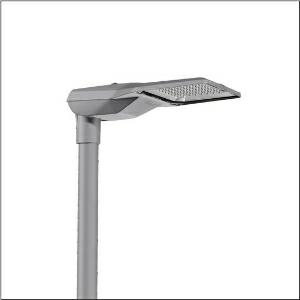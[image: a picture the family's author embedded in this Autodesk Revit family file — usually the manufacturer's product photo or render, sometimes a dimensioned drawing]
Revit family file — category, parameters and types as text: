
# Revit family: streetlight_sl_21_iq_midi___st1_0ab_5xe3m31v08nb_f534
name_source: partatom
category: Lighting Fixtures
units: mm (PartAtom-declared; Revit-internal decimal feet)

## family parameters
Cut with Voids When Loaded = No
Host = Face
Light Source = No
Part Type = Normal
Room Calculation Point = No
Round Connector Dimension = Use Diameter
Shared = No

## types (1)
- --- (1 x LED, 18970 lm, 136.6 W, 3000K)
    Apparent Load = 137 VA
    CIE Flux Codes = 40 74 97 100 100
    Color Rendering = 70
    Color Temperature = 3000K
    Default Elevation = 1800 mm
    Description = Streetlight SL 21 iQ midi, mast luminaire, primary light control with lens, of PMMA, primary optical cover: cover, of toughened safety glass, transparent, light distribution: ST1.0aB, light emission: direct distribution, primary light characteristic: asymmetric, installation type: post-top, side-entry, LED, High Power LED, rated luminous flux: 18.970lm, luminous efficacy: 139lm/W, light colour: 730, colour temperature: 3000K, control gear: iQ-Street Remote, D4i with power reduction, control: pre-setting: logarithmic dimming characteristic, Street-Remote, Auto-Match, Temp-Guard, Lumen-Switch, Night-Set, Smart-Wire, Light-Fading, Desk-Remote (wireless, voltage-free reading and setting of iQ features in the workshop via application-optimized NFC function/RFID function), optimised constant luminous flux control (CLO 2.0), mains connection: 230..240V, AC, 50/60Hz, start of lifetime: 137W, end of service life: 144W, reduction: 61W, luminaire housing, of diecast aluminium, powder-coated, SITECO metallic grey (DB 702S), corrosivity category C5 high according to DIN EN ISO 12944, please order mast flange separately, inclination adjustable: 0°, 5°, 10°, 15°, sealing non-destructively replaceable, multi-level sealing system, length: 644mm, width: 335mm, height: 110mm, mast flange for spigot size: 42mm (side-entry): 5XC10008XM4, 60/48mm (side-entry/post-top): 5XC10108XM2, 76/60mm (side-entry/post-top): 5XC10108XM1, mounting height: 4..8m, Smart Interface above, protection rating (complete): IP66, insulation class (complete): insulation class II (safety insulation), certification: CE, ENEC, ENEC+, VDE, impact resistance: IK10, permissible operating ambient temperature for outdoor applications: -40..+50°C, standard-compliant lighting for roads and squares, packaging unit: 1 piece

Light Distribution: ST1.0aB
    Height = 111 mm
    Lamp = 1 x LED
    Lamp Light Flux = 18970 lm
    Lamp Power = 136.6 W
    Lamp count = 1
    Length = 644 mm
    Luminous efficacy = 139 lm/W
    Manufacturer = Siteco
    ModVariant = No
    Model = 5XE3M31V08NB
    Number of Poles = 1
    OnlyDefault = Yes
    Power Factor = 1
    Product Name = Streetlight SL 21 iQ midi | ST1.0aB
    Product group = mast luminaire | pylon top
    ProductGroupID = 6100
    Protection Class = Protection class II
    Protection Degree = IP 66
    RLX_Detail_Level = 1
    RLX_Emergency_Light_Flux = 0 lm
    RLX_Emergency_Type = 0
    RLX_Emergency_Type_DB = No
    RlxData = <blob elided: 90797 chars, md5=cc77ea89>
    Socket = socket
    Standby Power = 0 W
    System Light Flux = 18970 lm
    System Power = 137 W
    Type Comments = factory setting: luminous flux: 100 % | dim-lin: 254 | 733 mA
    Type Image = l_1004302.jpg
    URL = http://relux.com
    VarID = @adj_112087
    Voltage = 0 V
    Weight = 0.00 kg
    Width = 336 mm

## geometry (parser evidence)
native form markers: Blend x4, Sweep x10
no freeform markers — native parametric forms only
